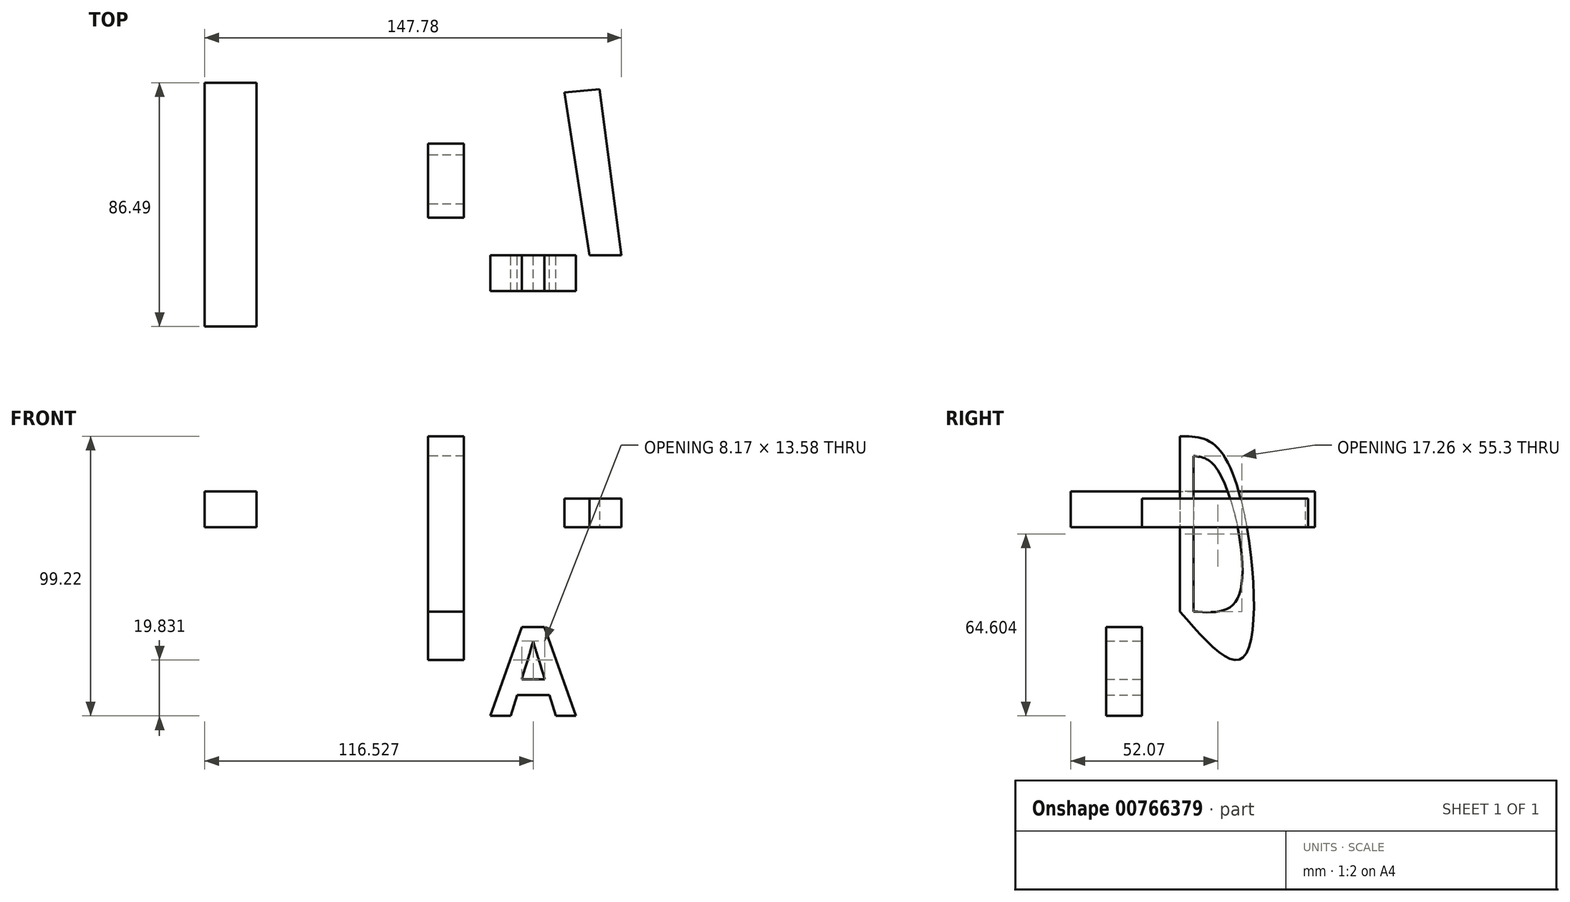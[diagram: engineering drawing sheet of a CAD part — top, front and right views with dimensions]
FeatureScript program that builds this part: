
annotation { "Feature Type Name" : "Feature", "Feature Type Description" : "" }
export const myFeature = defineFeature(function(context is Context, id is Id, definition is map)
    precondition{}
    {
        {
            var Q0;
            Q0=qCreatedBy(makeId("Top.planeOp"),FACE);
            var sketch = newSketch(context, id + "F0", { "sketchPlane" : qUnion([Q0])});
            skText(sketch, "E0", { "text": "I", "fontName": "OpenSans-Bold.ttf"});
            const initialGuessF0  = {"E0": [-0.0901, -0.02527, 1, 0, 0.08723]};
            skSetInitialGuess(sketch, initialGuessF0);
            skSolve(sketch);
        }
        {
            var Q0;
            Q0=makeQuery(id+"F0.imprint","IMPRINT",FACE,{"disambiguationData":[TD([[makeQuery(id+"F0.imprint","IMPRINT",EDGE,{"derivedFrom":sQuery(id+"F0.wireOp",EDGE,"E0.sketch_text.stroke-0")}),-1.0]])]});
            var Q1;
            Q1 = qSketchRegion(id + "F0", true);
            extrude(context, id + "F1", {"entities" : qUnion([Q0, Q1]), "depth" : 12.7 * mm, "offsetDistance" : 25.4 * mm});
        }
        {
            var Q0;
            Q0=qCreatedBy(makeId("Front.planeOp"),FACE);
            var sketch = newSketch(context, id + "F2", { "sketchPlane" : qUnion([Q0])});
            skLineSegment(sketch, "E1", {"start": v(-22.9, 42.06) * mm, "end": v(-22.9, -19.8) * mm});
            skLineSegment(sketch, "E2", {"start": v(-22.9, 42.06) * mm, "end": v(0, -10.78) * mm});
            skLineSegment(sketch, "E3", {"start": v(0, -10.78) * mm, "end": v(0, 45.04) * mm});
            skSolve(sketch);
        }
        {
            var Q0;
            Q0=sQuery(id+"F2.wireOp",EDGE,"E1");
            var Q1;
            Q1=sQuery(id+"F2.wireOp",EDGE,"E2");
            var Q2;
            Q2=sQuery(id+"F2.wireOp",EDGE,"E3");
            extrude(context, id + "F3", {"bodyType" : ToolBodyType.SURFACE, "surfaceEntities" : qUnion([Q0, Q1, Q2]), "depth" : 12.7 * mm, "offsetDistance" : 25.4 * mm});
        }
        {
            var Q0;
            Q0=qCreatedBy(makeId("Right.planeOp"),FACE);
            var sketch = newSketch(context, id + "F4", { "sketchPlane" : qUnion([Q0])});
            skLineSegment(sketch, "E4", {"start": v(13.35, 32.2) * mm, "end": v(13.35, -29.95) * mm});
            skFitSpline(sketch, "E5", {"points": [v(13.35, 32.2) * mm, v(29.56, 24.47) * mm, v(36.12, -45.93) * mm, v(13.35, -29.95) * mm], "startDerivative": vector(73.46, 0.95) * mm, "endDerivative": vector(-93.08, 106.52) * mm});
            skLineSegment(sketch, "E6", {"start": v(18.17, 25.23) * mm, "end": v(18.17, -29.95) * mm});
            skFitSpline(sketch, "E7", {"points": [v(18.17, 25.23) * mm, v(26.5, 20.7) * mm, v(33.93, -25.12) * mm, v(18.17, -29.95) * mm], "startDerivative": vector(37.83, -3.57) * mm, "endDerivative": vector(-67.07, 4.83) * mm});
            skSolve(sketch);
        }
        {
            var Q0;
            Q0 = qSketchRegion(id + "F4", true);
            extrude(context, id + "F5", {"entities" : qUnion([Q0]), "depth" : 12.7 * mm, "offsetDistance" : 25.4 * mm});
        }
        {
            var Q0;
            Q0=qCreatedBy(makeId("Top.planeOp"),FACE);
            var sketch = newSketch(context, id + "F6", { "sketchPlane" : qUnion([Q0])});
            skLineSegment(sketch, "E8", {"start": v(48.35, 57.83) * mm, "end": v(57.21, 0) * mm});
            skLineSegment(sketch, "E9", {"start": v(68.56, 0) * mm, "end": v(60.82, 58.93) * mm});
            skLineSegment(sketch, "E10", {"start": v(60.82, 58.93) * mm, "end": v(48.35, 57.83) * mm});
            skLineSegment(sketch, "E11", {"start": v(68.56, 0) * mm, "end": v(57.21, 0) * mm});
            skSolve(sketch);
        }
        {
            var Q0;
            Q0=makeQuery(id+"F6.imprint","IMPRINT",FACE,{"disambiguationData":[TD([[makeQuery(id+"F6.imprint","IMPRINT",EDGE,{"derivedFrom":sQuery(id+"F6.wireOp",EDGE,"E8")}),1.0]])]});
            extrude(context, id + "F7", {"entities" : qUnion([Q0]), "depth" : 10.16 * mm, "offsetDistance" : 25.4 * mm});
        }
        {
            var Q0;
            Q0=qCreatedBy(makeId("Front.planeOp"),FACE);
            var sketch = newSketch(context, id + "F8", { "sketchPlane" : qUnion([Q0])});
            skText(sketch, "E12", { "text": "A", "fontName": "OpenSans-Bold.ttf"});
            const initialGuessF8  = {"E12": [0.02211, -0.06702, 1, 0, 0.03163]};
            skSetInitialGuess(sketch, initialGuessF8);
            skSolve(sketch);
        }
        {
            var Q0;
            Q0 = qSketchRegion(id + "F8", true);
            extrude(context, id + "F9", {"entities" : qUnion([Q0]), "depth" : 12.7 * mm, "offsetDistance" : 25.4 * mm});
        }
    });
